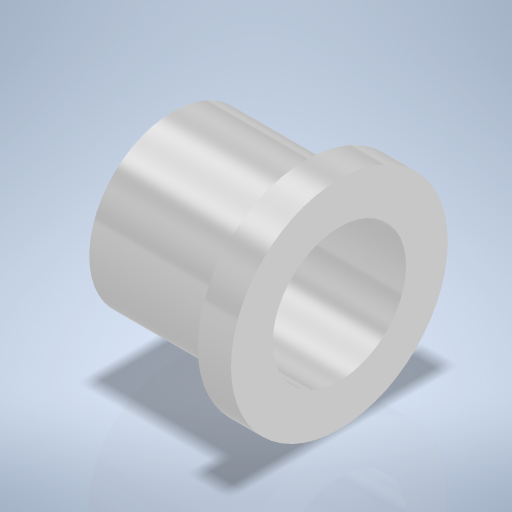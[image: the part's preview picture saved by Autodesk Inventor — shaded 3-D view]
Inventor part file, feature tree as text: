
AUTODESK INVENTOR PART (.ipt)
format: ipt  version: 2024 (Build 280153000, 153)  size: 253,952 bytes
history: native  units: mm
features: sketch x2, revolve x1, hole x1
ambient origin geometry x8: Origin, YZ Plane, XZ Plane, XY Plane, X Axis, Y Axis, Z Axis, Center Point
bodies: Volumenkörper1 (feature_tree)
feature tree (4):
  revolve  "Umdrehung1"
  hole  "Bohrung1"  [1 undecoded]
  sketch  "Skizze1"  dims[d0=2.0mm d1=8.0mm]
  sketch  "Skizze2"  dims[d2=10.0mm d3=13.0mm d4=90.0deg d5=8.0mm d6=6.0mm d7=4.0mm d8=2.0mm d9=90.0deg d10=26.0mm d11=0.0mm]
note: 1 required parameter value undecoded (feature->parameter linkage not recoverable at this tier; creation-order binding heuristic only, values carry confidence <= 0.55)
